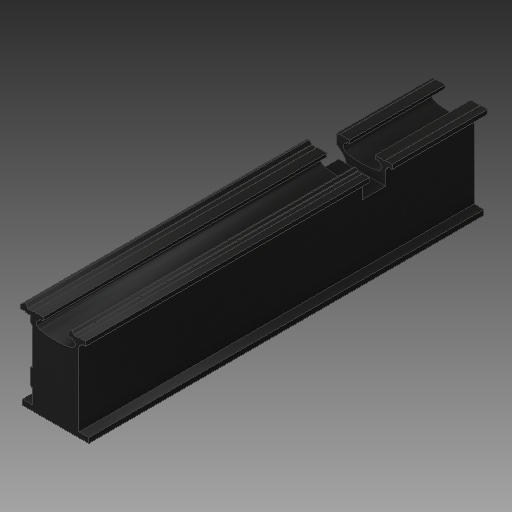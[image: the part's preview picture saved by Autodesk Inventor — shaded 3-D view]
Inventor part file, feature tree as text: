
AUTODESK INVENTOR PART (.ipt)
format: ipt  version: 2018 (Build 220112000, 112)  size: 455,168 bytes
history: native  units: in
note: dims shown in document units (in); Inventor stores cm internally (conversion verified against a paired STEP export)
features: sketch x13, extrude x12, reference x6, plane x3, chamfer x1
ambient origin geometry x8: Origin, YZ Plane, XZ Plane, XY Plane, X Axis, Y Axis, Z Axis, Center Point
bodies: Solid1 (feature_tree)
feature tree (35):
  extrude  "Extrusion1"  TaperAngle=150.0deg  [1 undecoded]
  chamfer  "Chamfer1"  Distance=0.5787in
  plane  "Work Plane3"
  extrude  "Extrusion2"  Depth=0.3937in
  extrude  "Extrusion3"  TaperAngle=120.0deg  [1 undecoded]
  extrude  "Extrusion4"  Depth=0.1575in
  extrude  "Extrusion5"  Depth=0.3937in
  extrude  "Extrusion6"  Depth=0.3937in
  extrude  "Extrusion7"  Depth=0.3937in
  extrude  "Extrusion8"  Depth=0.3937in
  plane  "Work Plane4"
  plane  "Work Plane5"
  extrude  "Extrusion9"  Depth=0.3937in
  extrude  "Extrusion10"  TaperAngle=180.0deg  [1 undecoded]
  extrude  "Extrusion11"  Depth=0.3937in
  extrude  "Extrusion12"  Depth=0.3937in
  sketch  "Sketch14"  dims[d13=0.6181in d14=0.5787in d15=0.315in d16=120.0deg d17=0.1575in d18=2.4409in d19=8.0315in d22=3.6299in d24=0.5in d25=1.4252in d26=180.0deg d27=0.0787in d28=0.748in d29=0.0787in d30=0.5197in d31=0.962in d32=0.1811in d33=0.6299in d34=0.962in d35=0.5512in d36=0.5512in d37=90.0deg d38=0.1181in d39=60.0deg d40=0.685in d41=0.8858in d43=5.2953in d44=90.0deg d46=2.185in d47=90.0deg d50=90.0deg d51=1.378in d52=180.0deg d53=0.7087in d54=90.0deg d55=1.378in d57=0.7087in d59=180.0deg d60=0.315in d61=120.0deg d62=2.4409in d63=55.9055in d64=0.0in d65=0.1575in d66=0.0787in d67=45.0deg d68=40.1575in d69=3.2283in d70=3.4528in d71=55.9055in d72=0.0in d73=55.9055in d74=0.0in d75=55.9055in d76=0.0in d77=3.3465in d78=1.2205in d79=1.7323in d80=55.9055in d81=0.0in d82=1.0236in d83=0.0in d84=0.315in d85=0.315in d86=0.7283in d87=0.5512in d88=0.5118in d89=0.3937in d90=0.0in d91=0.315in d92=0.315in d93=6.7717in d94=0.8858in d95=0.5512in d96=0.7874in d97=0.0in d98=0.2756in d99=0.3937in d100=0.0in d101=5.5118in d102=1.9685in d103=0.2756in d104=1.5748in d105=0.0787in d106=0.0in d107=0.7874in d108=0.0in d112=0.315in d113=1.9685in d114=0.0in d115=0.0in]
  sketch  "Sketch1"  dims[d0=0.4331in d1=150.0deg]
  sketch  "Sketch2"  dims[d2=0.3937in]
  sketch  "Sketch3"  dims[d3=0.4606in]
  sketch  "Sketch4"  dims[d4=0.4961in]
  sketch  "Sketch5"  dims[d5=0.962in]
  sketch  "Sketch6"  dims[d6=0.1496in]
  sketch  "Sketch8"  dims[d7=0.4016in]
  sketch  "Sketch9"  dims[d8=0.962in]
  sketch  "Sketch10"  dims[d9=0.126in]
  sketch  "Sketch11"  dims[d10=0.6339in]
  sketch  "Sketch12"  dims[d11=0.0787in]
  reference  "Reference1"
  reference  "Reference2"
  reference  "Reference3"
  reference  "Reference4"
  reference  "Reference5"
  reference  "Reference6"
  sketch  "Sketch13"  dims[d12=0.9921in]
note: 3 required parameter values undecoded (feature->parameter linkage not recoverable at this tier; creation-order binding heuristic only, values carry confidence <= 0.55)
